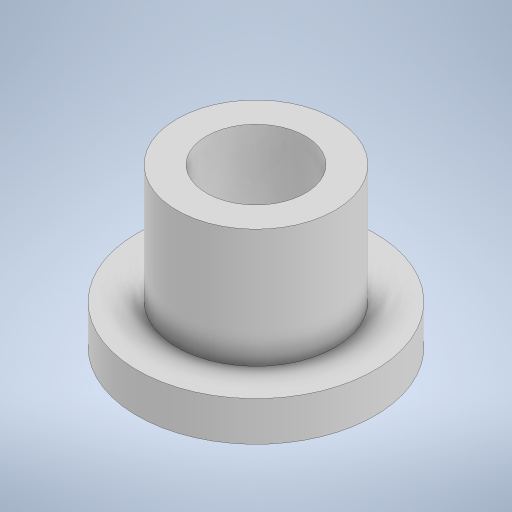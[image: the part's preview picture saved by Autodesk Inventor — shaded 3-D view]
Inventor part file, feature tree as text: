
AUTODESK INVENTOR PART (.ipt)
format: ipt  version: 2024.2 (Build 282272000, 272)  size: 218,112 bytes
history: native  units: mm
features: extrude x2, other x1, sketch x1
ambient origin geometry x8: Origin, YZ Plane, XZ Plane, XY Plane, X Axis, Y Axis, Z Axis, Center Point
bodies: Body1 (feature_tree)
feature tree (4):
  other  "Твердое тело1"
  sketch  "Эскиз1"
  extrude  "Выдавливание1"  Depth=5.0mm
  extrude  "Выдавливание2"  Depth=8.0mm
